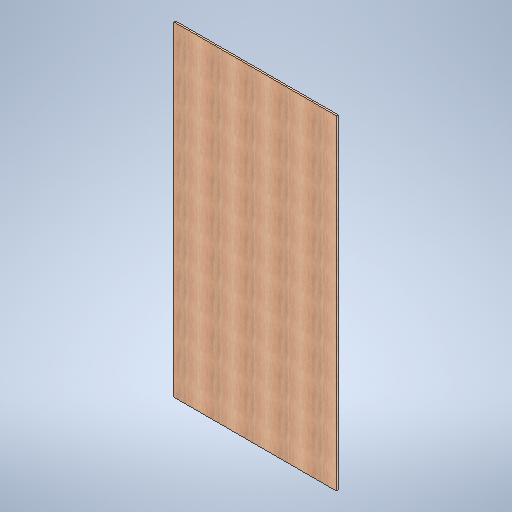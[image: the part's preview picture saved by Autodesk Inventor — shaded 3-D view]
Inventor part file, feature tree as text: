
AUTODESK INVENTOR PART (.ipt)
format: ipt  version: 2025 (Build 290162010, 162A)  size: 359,936 bytes
history: native  units: in
note: dims shown in document units (in); Inventor stores cm internally (conversion verified against a paired STEP export)
features: extrude x1, sketch x1
ambient origin geometry x8: Origin, YZ Plane, XZ Plane, XY Plane, X Axis, Y Axis, Z Axis, Center Point
bodies: Solid1 (feature_tree)
feature tree (2):
  extrude  "Extrusion1"  Depth=48.0in
  sketch  "Sketch1"  dims[d2=96.0in d3=48.0in d4=0.5in d5=0.0in]
